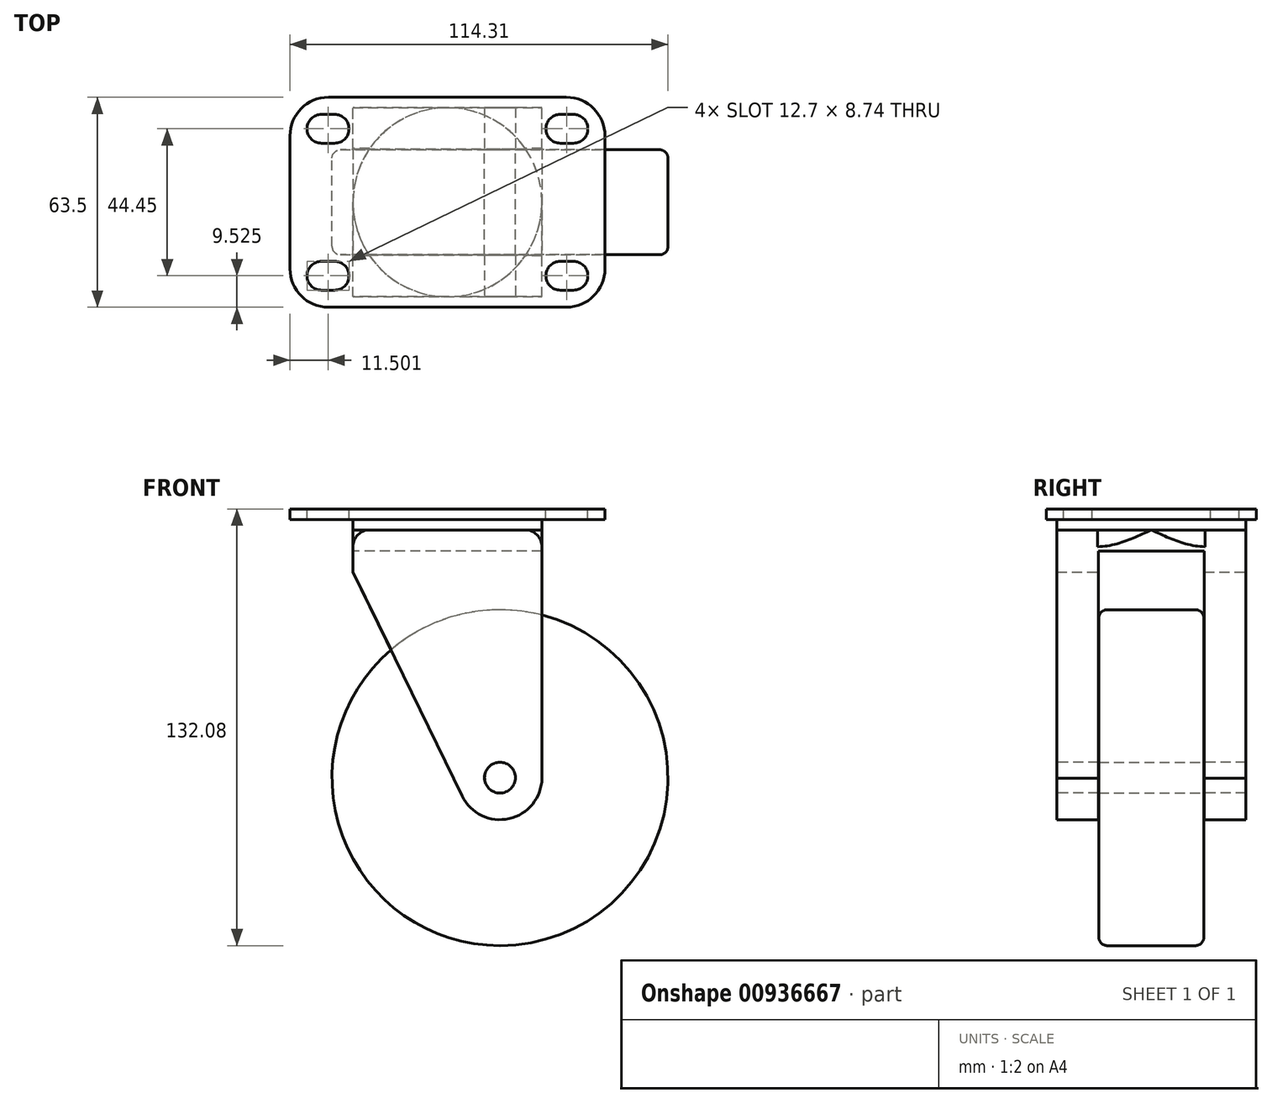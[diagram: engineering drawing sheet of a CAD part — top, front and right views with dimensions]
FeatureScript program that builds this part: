
annotation { "Feature Type Name" : "Feature", "Feature Type Description" : "" }
export const myFeature = defineFeature(function(context is Context, id is Id, definition is map)
    precondition{}
    {
        {
            var Q0;
            Q0=qCreatedBy(makeId("Top.planeOp"),FACE);
            var sketch = newSketch(context, id + "F0", { "sketchPlane" : qUnion([Q0])});
            skLineSegment(sketch, "E0.bottom", {"start": v(-47.62, 31.75) * mm, "end": v(47.63, 31.75) * mm});
            skLineSegment(sketch, "E0.top", {"start": v(-47.62, -31.75) * mm, "end": v(47.63, -31.75) * mm});
            skLineSegment(sketch, "E0.left", {"start": v(-47.62, 31.75) * mm, "end": v(-47.63, -31.75) * mm});
            skLineSegment(sketch, "E0.right", {"start": v(47.63, 31.75) * mm, "end": v(47.62, -31.75) * mm});
            skPoint(sketch, "E0.middle", {"position": v(0, 0) * mm});
            skArc(sketch, "E1", {"start": v(-38.1, -17.86) * mm, "mid": v(-42.47, -22.23) * mm, "end": v(-38.1, -26.6) * mm});
            skArc(sketch, "E2", {"start": v(-34.14, -26.6) * mm, "mid": v(-29.77, -22.23) * mm, "end": v(-34.14, -17.86) * mm});
            skLineSegment(sketch, "E3", {"start": v(-38.1, -26.6) * mm, "end": v(-34.14, -26.6) * mm});
            skLineSegment(sketch, "E4", {"start": v(-34.14, -17.86) * mm, "end": v(-38.1, -17.86) * mm});
            skArc(sketch, "E5.MirrorCS", {"start": v(-38.1, 17.86) * mm, "mid": v(-42.47, 22.23) * mm, "end": v(-38.1, 26.6) * mm});
            skLineSegment(sketch, "E6.MirrorCS", {"start": v(-34.14, 17.86) * mm, "end": v(-38.1, 17.86) * mm});
            skLineSegment(sketch, "E7.MirrorCS", {"start": v(-38.1, 26.6) * mm, "end": v(-34.14, 26.6) * mm});
            skArc(sketch, "E8.MirrorCS", {"start": v(-34.14, 26.6) * mm, "mid": v(-29.77, 22.23) * mm, "end": v(-34.14, 17.86) * mm});
            skLineSegment(sketch, "E9.MirrorCS", {"start": v(34.14, -17.86) * mm, "end": v(38.1, -17.86) * mm});
            skLineSegment(sketch, "E10.MirrorCS", {"start": v(38.1, -26.6) * mm, "end": v(34.14, -26.6) * mm});
            skArc(sketch, "E11.MirrorCS", {"start": v(34.14, -26.6) * mm, "mid": v(29.77, -22.23) * mm, "end": v(34.14, -17.86) * mm});
            skLineSegment(sketch, "E12.MirrorCS", {"start": v(38.1, 26.6) * mm, "end": v(34.14, 26.6) * mm});
            skLineSegment(sketch, "E13.MirrorCS", {"start": v(34.14, 17.86) * mm, "end": v(38.1, 17.86) * mm});
            skArc(sketch, "E14.MirrorCS", {"start": v(34.14, 26.6) * mm, "mid": v(29.77, 22.23) * mm, "end": v(34.14, 17.86) * mm});
            skLineSegment(sketch, "E15.MirrorCS", {"start": v(47.62, 31.75) * mm, "end": v(47.63, -31.75) * mm});
            skLineSegment(sketch, "E16.MirrorCS", {"start": v(47.62, -31.75) * mm, "end": v(-47.63, -31.75) * mm});
            skArc(sketch, "E17.MirrorCS", {"start": v(38.1, -17.86) * mm, "mid": v(42.47, -22.23) * mm, "end": v(38.1, -26.6) * mm});
            skLineSegment(sketch, "E18.MirrorCS", {"start": v(47.62, 31.75) * mm, "end": v(-47.63, 31.75) * mm});
            skArc(sketch, "E19.MirrorCS", {"start": v(38.1, 17.86) * mm, "mid": v(42.47, 22.23) * mm, "end": v(38.1, 26.6) * mm});
            skSolve(sketch);
        }
        {
            var Q0;
            Q0=makeQuery(id+"F0.imprint","IMPRINT",FACE,{"disambiguationData":[TD([[makeQuery(id+"F0.imprint","IMPRINT",EDGE,{"derivedFrom":sQuery(id+"F0.wireOp",EDGE,"E0.left")}),1.0]])]});
            extrude(context, id + "F1", {"entities" : qUnion([Q0]), "oppositeDirection" : true, "depth" : 3.17 * mm, "offsetDistance" : 25.4 * mm});
        }
        {
            var Q0;
            Q0=makeQuery(id+"F1.opExtrude","CAP_FACE",FACE,{"disambiguationData":[OSD([sQuery(id+"F0.wireOp",EDGE,"E0.left"),sQuery(id+"F0.wireOp",EDGE,"E1"),sQuery(id+"F0.wireOp",EDGE,"E2"),sQuery(id+"F0.wireOp",EDGE,"E3"),sQuery(id+"F0.wireOp",EDGE,"E4"),sQuery(id+"F0.wireOp",EDGE,"E5.MirrorCS"),sQuery(id+"F0.wireOp",EDGE,"E6.MirrorCS"),sQuery(id+"F0.wireOp",EDGE,"E7.MirrorCS"),sQuery(id+"F0.wireOp",EDGE,"E8.MirrorCS"),sQuery(id+"F0.wireOp",EDGE,"E10.MirrorCS"),sQuery(id+"F0.wireOp",EDGE,"E9.MirrorCS"),sQuery(id+"F0.wireOp",EDGE,"E12.MirrorCS"),sQuery(id+"F0.wireOp",EDGE,"E13.MirrorCS"),sQuery(id+"F0.wireOp",EDGE,"E11.MirrorCS"),sQuery(id+"F0.wireOp",EDGE,"E14.MirrorCS"),sQuery(id+"F0.wireOp",EDGE,"E15.MirrorCS"),sQuery(id+"F0.wireOp",EDGE,"E16.MirrorCS"),sQuery(id+"F0.wireOp",EDGE,"E17.MirrorCS"),sQuery(id+"F0.wireOp",EDGE,"E18.MirrorCS"),sQuery(id+"F0.wireOp",EDGE,"E19.MirrorCS")])],"isStart":false});
            var sketch = newSketch(context, id + "F2", { "sketchPlane" : qUnion([Q0])});
            skCircle(sketch, "E20", {"center": v(0, 0) * mm, "radius": 28.57 * mm});
            skSolve(sketch);
        }
        {
            var Q0;
            Q0=makeQuery(id+"F2.imprint","IMPRINT",FACE,{"disambiguationData":[TD([[makeQuery(id+"F2.imprint","IMPRINT",EDGE,{"derivedFrom":sQuery(id+"F2.wireOp",EDGE,"E20")}),1.0]])]});
            extrude(context, id + "F3", {"entities" : qUnion([Q0]), "operationType" : NewBodyOperationType.ADD, "depth" : 3.17 * mm, "offsetDistance" : 25.4 * mm});
        }
        {
            var Q0;
            Q0=qCreatedBy(makeId("Front.planeOp"),FACE);
            var sketch = newSketch(context, id + "F4", { "sketchPlane" : qUnion([Q0])});
            skLineSegment(sketch, "E21.bottom", {"start": v(28.58, -6.35) * mm, "end": v(-28.57, -6.35) * mm});
            skLineSegment(sketch, "E21.top", {"start": v(28.58, -19.05) * mm, "end": v(-28.57, -19.05) * mm});
            skLineSegment(sketch, "E21.left", {"start": v(28.58, -6.35) * mm, "end": v(28.58, -19.05) * mm});
            skLineSegment(sketch, "E21.right", {"start": v(-28.57, -6.35) * mm, "end": v(-28.57, -19.05) * mm});
            skArc(sketch, "E22", {"start": v(4.46, -86.84) * mm, "mid": v(18.83, -93.63) * mm, "end": v(28.57, -81.07) * mm});
            skLineSegment(sketch, "E23", {"start": v(28.57, -81.49) * mm, "end": v(28.58, -19.05) * mm});
            skLineSegment(sketch, "E24", {"start": v(-28.58, -19.05) * mm, "end": v(4.46, -86.84) * mm});
            skSolve(sketch);
        }
        {
            var Q0;
            {var subQ1=sQuery(id+"F4.wireOp",EDGE,"E21.top");Q0=makeQuery(id+"F4.imprint","IMPRINT",FACE,{"disambiguationData":[TD([[makeQuery(id+"F4.imprint","IMPRINT",EDGE,{"derivedFrom":subQ1}),1.0]])]});}
            var Q1;
            Q1=makeQuery(id+"F4.imprint","IMPRINT",FACE,{"disambiguationData":[TD([[makeQuery(id+"F4.imprint","IMPRINT",EDGE,{"derivedFrom":sQuery(id+"F4.wireOp",EDGE,"E21.bottom")}),1.0]])]});
            extrude(context, id + "F5", {"entities" : qUnion([Q0, Q1]), "operationType" : NewBodyOperationType.ADD, "depth" : 28.57 * mm, "offsetDistance" : 25.4 * mm, "hasSecondDirection" : true, "secondDirectionOppositeDirection" : true, "secondDirectionDepth" : 28.57 * mm});
        }
        {
            var Q0;
            Q0=qCreatedBy(makeId("Right.planeOp"),FACE);
            var sketch = newSketch(context, id + "F6", { "sketchPlane" : qUnion([Q0])});
            skLineSegment(sketch, "E25.bottom", {"start": v(-16, -125.42) * mm, "end": v(16, -125.42) * mm});
            skLineSegment(sketch, "E25.top", {"start": v(-16, -12.7) * mm, "end": v(16, -12.7) * mm});
            skLineSegment(sketch, "E25.left", {"start": v(-16, -125.42) * mm, "end": v(-16, -12.7) * mm});
            skLineSegment(sketch, "E25.right", {"start": v(16, -125.42) * mm, "end": v(16, -12.7) * mm});
            skSolve(sketch);
        }
        {
            var Q0;
            Q0=qSketchRegion(id+"F6",true);
            extrude(context, id + "F7", {"entities" : qUnion([Q0]), "operationType" : NewBodyOperationType.REMOVE, "depth" : 50.8 * mm, "offsetDistance" : 25.4 * mm, "hasSecondDirection" : true, "secondDirectionOppositeDirection" : true, "secondDirectionDepth" : 50.8 * mm});
        }
        {
            var Q0;
            Q0=makeQuery(id+"F5.opExtrude","CAP_FACE",FACE,{"disambiguationData":[OSD([sQuery(id+"F4.wireOp",EDGE,"E21.bottom"),sQuery(id+"F4.wireOp",EDGE,"E21.left"),sQuery(id+"F4.wireOp",EDGE,"E21.right"),sQuery(id+"F4.wireOp",EDGE,"E22"),sQuery(id+"F4.wireOp",EDGE,"E23"),sQuery(id+"F4.wireOp",EDGE,"E24")])],"isStart":false});
            var sketch = newSketch(context, id + "F8", { "sketchPlane" : qUnion([Q0])});
            skPoint(sketch, "E26", {"position": v(15.88, -81.28) * mm});
            skSolve(sketch);
        }
        {
            var Q0;
            Q0=sQuery(id+"F8.wireOp",VERTEX,"E26");
            var Q1;
            Q1=makeQuery(id+"F1.opExtrude","SWEPT_BODY",BODY,{"disambiguationData":[OSD([sQuery(id+"F0.wireOp",EDGE,"E0.left"),sQuery(id+"F0.wireOp",EDGE,"E1"),sQuery(id+"F0.wireOp",EDGE,"E2"),sQuery(id+"F0.wireOp",EDGE,"E3"),sQuery(id+"F0.wireOp",EDGE,"E4"),sQuery(id+"F0.wireOp",EDGE,"E5.MirrorCS"),sQuery(id+"F0.wireOp",EDGE,"E6.MirrorCS"),sQuery(id+"F0.wireOp",EDGE,"E7.MirrorCS"),sQuery(id+"F0.wireOp",EDGE,"E8.MirrorCS"),sQuery(id+"F0.wireOp",EDGE,"E10.MirrorCS"),sQuery(id+"F0.wireOp",EDGE,"E9.MirrorCS"),sQuery(id+"F0.wireOp",EDGE,"E12.MirrorCS"),sQuery(id+"F0.wireOp",EDGE,"E13.MirrorCS"),sQuery(id+"F0.wireOp",EDGE,"E11.MirrorCS"),sQuery(id+"F0.wireOp",EDGE,"E14.MirrorCS"),sQuery(id+"F0.wireOp",EDGE,"E15.MirrorCS"),sQuery(id+"F0.wireOp",EDGE,"E16.MirrorCS"),sQuery(id+"F0.wireOp",EDGE,"E17.MirrorCS"),sQuery(id+"F0.wireOp",EDGE,"E18.MirrorCS"),sQuery(id+"F0.wireOp",EDGE,"E19.MirrorCS")])]});
            hole(context, id + "F9", {"style" : HoleStyle.SIMPLE, "endStyle" : HoleEndStyle.THROUGH, "standardTappedOrClearance" : lookupTablePath({ "standard" : "ANSI", "engagement" : "75%", "pitch" : "14 tpi", "size" : "7/16", "type" : "Tapped" }), "standardBlindInLast" : lookupTablePath({ "standard" : "ANSI", "engagement" : "75%", "pitch" : "14 tpi", "size" : "7/16", "type" : "Tapped" }), "holeDiameter" : 9.35 * mm, "majorDiameter" : 11.1 * mm, "showTappedDepth" : true, "isTappedThrough" : true, "tappedDepth" : 12.71 * mm, "tapClearance" : 3, "startFromSketch" : true, "locations" : qUnion([Q0]), "scope" : qUnion([Q1])});
        }
        {
            var Q0;
            {var subQ0=sQuery(id+"F4.wireOp",EDGE,"E21.bottom");var subQ1=sQuery(id+"F4.wireOp",EDGE,"E21.right");Q0=makeQuery(id+"F5.boolean.opBoolean","SPLIT",EDGE,{"disambiguationData":[TD([makeQuery(id+"F5.opExtrude","CAP_FACE",FACE,{"disambiguationData":[OSD([subQ0,sQuery(id+"F4.wireOp",EDGE,"E21.left"),subQ1,sQuery(id+"F4.wireOp",EDGE,"E22"),sQuery(id+"F4.wireOp",EDGE,"E23"),sQuery(id+"F4.wireOp",EDGE,"E24")])],"isStart":false})])],"derivedFrom":makeQuery(id+"F5.opExtrude","SWEPT_EDGE",EDGE,{"disambiguationData":[OSD([subQ0,subQ1])]})});}
            var Q1;
            {var subQ0=sQuery(id+"F4.wireOp",EDGE,"E21.bottom");var subQ1=sQuery(id+"F4.wireOp",EDGE,"E21.left");Q1=makeQuery(id+"F5.boolean.opBoolean","SPLIT",EDGE,{"disambiguationData":[TD([makeQuery(id+"F5.opExtrude","CAP_FACE",FACE,{"disambiguationData":[OSD([subQ0,subQ1,sQuery(id+"F4.wireOp",EDGE,"E21.right"),sQuery(id+"F4.wireOp",EDGE,"E22"),sQuery(id+"F4.wireOp",EDGE,"E23"),sQuery(id+"F4.wireOp",EDGE,"E24")])],"isStart":false})])],"derivedFrom":makeQuery(id+"F5.opExtrude","SWEPT_EDGE",EDGE,{"disambiguationData":[OSD([subQ0,subQ1])]})});}
            fillet(context, id + "F10", {"entities" : qUnion([Q0, Q1]), "radius" : 5.08 * mm, "tangentPropagation" : true, "allowEdgeOverflow" : false});
        }
        {
            var Q0;
            Q0=makeQuery(id+"F1.opExtrude","SWEPT_EDGE",EDGE,{"disambiguationData":[OSD([sQuery(id+"F0.wireOp",EDGE,"E15.MirrorCS"),sQuery(id+"F0.wireOp",EDGE,"E16.MirrorCS")])]});
            var Q1;
            Q1=makeQuery(id+"F1.opExtrude","SWEPT_EDGE",EDGE,{"disambiguationData":[OSD([sQuery(id+"F0.wireOp",EDGE,"E15.MirrorCS"),sQuery(id+"F0.wireOp",EDGE,"E18.MirrorCS")])]});
            var Q2;
            Q2=makeQuery(id+"F1.opExtrude","SWEPT_EDGE",EDGE,{"disambiguationData":[OSD([sQuery(id+"F0.wireOp",EDGE,"E0.left"),sQuery(id+"F0.wireOp",EDGE,"E18.MirrorCS")])]});
            var Q3;
            Q3=makeQuery(id+"F1.opExtrude","SWEPT_EDGE",EDGE,{"disambiguationData":[OSD([sQuery(id+"F0.wireOp",EDGE,"E0.left"),sQuery(id+"F0.wireOp",EDGE,"E16.MirrorCS")])]});
            fillet(context, id + "F11", {"entities" : qUnion([Q0, Q1, Q2, Q3]), "radius" : 11.65 * mm, "tangentPropagation" : true, "allowEdgeOverflow" : false});
        }
        {
            var Q0;
            Q0=qCreatedBy(makeId("Front.planeOp"),FACE);
            var sketch = newSketch(context, id + "F12", { "sketchPlane" : qUnion([Q0])});
            skCircle(sketch, "E27", {"center": v(15.89, -81.28) * mm, "radius": 50.8 * mm});
            skCircle(sketch, "E28", {"center": v(15.89, -81.28) * mm, "radius": 4.67 * mm});
            skSolve(sketch);
        }
        {
            var Q0;
            Q0=makeQuery(id+"F12.imprint","IMPRINT",FACE,{"disambiguationData":[TD([[makeQuery(id+"F12.imprint","IMPRINT",EDGE,{"derivedFrom":sQuery(id+"F12.wireOp",EDGE,"E27")}),1.0]])]});
            extrude(context, id + "F13", {"entities" : qUnion([Q0]), "depth" : 15.88 * mm, "offsetDistance" : 25.4 * mm, "hasSecondDirection" : true, "secondDirectionOppositeDirection" : true, "secondDirectionDepth" : 15.88 * mm});
        }
        {
            var Q0;
            Q0=makeQuery(id+"F13.opExtrude","CAP_EDGE",EDGE,{"disambiguationData":[OSD([sQuery(id+"F12.wireOp",EDGE,"E27")])],"isStart":false});
            var Q1;
            Q1=makeQuery(id+"F13.opExtrude","CAP_EDGE",EDGE,{"disambiguationData":[OSD([sQuery(id+"F12.wireOp",EDGE,"E27")])],"isStart":true});
            fillet(context, id + "F14", {"entities" : qUnion([Q0, Q1]), "radius" : 2.54 * mm, "tangentPropagation" : true, "allowEdgeOverflow" : false});
        }
    });
